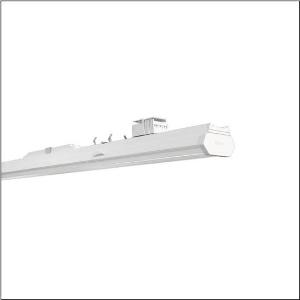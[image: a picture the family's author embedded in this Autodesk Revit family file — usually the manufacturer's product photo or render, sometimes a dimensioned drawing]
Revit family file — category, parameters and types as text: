
# Revit family: licross_r__11_protected_mo_51tp12mn4axg_95e7
name_source: partatom
category: Lighting Fixtures
units: mm (PartAtom-declared; Revit-internal decimal feet)

## family parameters
Cut with Voids When Loaded = No
Host = Face
Light Source = No
Part Type = Normal
Room Calculation Point = No
Round Connector Dimension = Use Diameter
Shared = No

## types (1)
- --- (1 x LED, 10020 lm, 55.3 W, 4000K)
    Apparent Load = 55 VA
    CIE Flux Codes = 73 92 98 99 100
    Color Rendering = 80
    Color Temperature = 4000K
    Default Elevation = 1800 mm
    Description = Licross® 11 Protected MO, luminaire insert, of sheet steel, galvanised, coil coated, white, length: 1.500mm, width: 90mm, height: 101mm, LED rated luminous flux: 10.030lm, light colour: 840, control gear: ON/OFF Multilumen, with plug, 3-pole, with phase selection, mains connection: 220..240V, AC, 50/60Hz, rated input power: 55W, halogen-free wiring, primary light control with lens, of plastic, primary optical cover: cover, of PMMA, light emission: direct distribution, primary light characteristic: symmetric, protection rating (complete): IP64, insulation class (complete): insulation class I (protective earthing), certification: CE, ENEC, VDE, UKCA, protection symbol: D if used in an environment with conductive dust loads with corresponding accessories, impact resistance: IK06, permissible ambient temperature for indoor applications: -35..+40°C, corresponds to IFS (International Featured Standards) requirements for safety and quality in the food industry, reducing of maximum allowable ambient temperature of 5°C with ceiling mounting, LABS conformity tested according to VDMA 24364:2018-05, packaging unit: 1 piece
    Height = 92 mm
    Lamp = 1 x LED
    Lamp Light Flux = 10020 lm
    Lamp Power = 55.3 W
    Lamp count = 1
    Length = 1500 mm
    Luminous efficacy = 181 lm/W
    Manufacturer = Siteco
    ModVariant = No
    Model = 51TP12MN4AXG
    Mounting Place = Ceiling
    Mounting Type = Pendant
    Number of Poles = 1
    OnlyDefault = Yes
    Power Factor = 1
    Product Name = Licross® 11 Protected MO
    Product group = luminaire insert
    ProductGroupID = 901
    Protection Class = Protection class I
    Protection Degree = IP 64
    RLX_Detail_Level = 1
    RLX_Emergency_Light_Flux = 0 lm
    RLX_Emergency_Type = 0
    RLX_Emergency_Type_DB = No
    RlxData = <blob elided: 22025 chars, md5=eaa7f02f>
    Socket = socket
    Standby Power = 0 W
    System Light Flux = 10020 lm
    System Power = 55 W
    Type Comments = factory setting: luminous flux: 100 % | (A | C | E) | 126 mA
    Type Image = l_1256148.jpg
    URL = http://relux.com
    VarID = @adj_019429
    Voltage = 0 V
    Weight = 0.00 kg
    Width = 88 mm

## geometry (parser evidence)
native form markers: Blend x4, Sweep x12
no freeform markers — native parametric forms only
